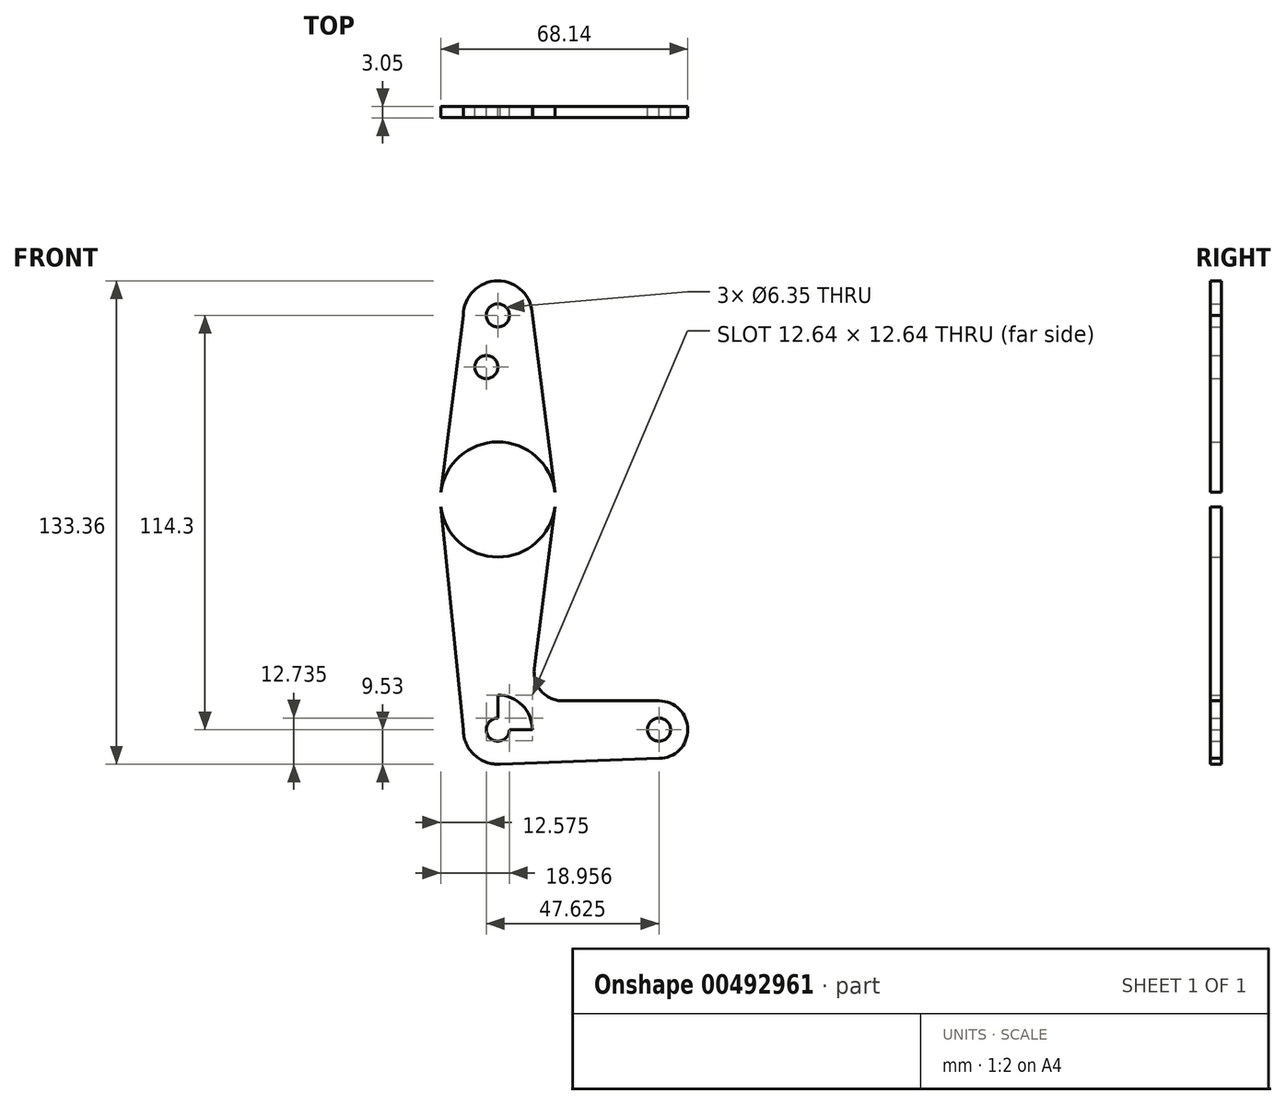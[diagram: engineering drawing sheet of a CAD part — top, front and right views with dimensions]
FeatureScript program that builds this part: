
annotation { "Feature Type Name" : "Feature", "Feature Type Description" : "" }
export const myFeature = defineFeature(function(context is Context, id is Id, definition is map)
    precondition{}
    {
        {
            var Q0;
            Q0=qCreatedBy(makeId("Front.planeOp"),FACE);
            var sketch = newSketch(context, id + "F0", { "sketchPlane" : qUnion([Q0])});
            skLineSegment(sketch, "E0", {"start": v(0, 0) * mm, "end": v(0, 114.3) * mm});
            skLineSegment(sketch, "E1", {"start": v(0, 114.3) * mm, "end": v(0, 0) * mm});
            skLineSegment(sketch, "E2", {"start": v(0, 0) * mm, "end": v(44.45, 0) * mm});
            skLineSegment(sketch, "E3", {"start": v(44.45, 0) * mm, "end": v(0, 0) * mm});
            skCircle(sketch, "E4", {"center": v(0, 114.3) * mm, "radius": 9.53 * mm});
            skCircle(sketch, "E5", {"center": v(0, 63.5) * mm, "radius": 15.88 * mm});
            skCircle(sketch, "E6", {"center": v(0, 0) * mm, "radius": 9.53 * mm});
            skCircle(sketch, "E7", {"center": v(44.45, 0) * mm, "radius": 7.94 * mm});
            skLineSegment(sketch, "E8", {"start": v(9.52, 114.3) * mm, "end": v(15.75, 65.5) * mm});
            skLineSegment(sketch, "E9", {"start": v(15.75, 61.5) * mm, "end": v(10.06, 16.9) * mm});
            skLineSegment(sketch, "E10", {"start": v(-9.52, 114.3) * mm, "end": v(-15.75, 65.5) * mm});
            skLineSegment(sketch, "E11", {"start": v(17.95, 7.94) * mm, "end": v(44.45, 7.94) * mm});
            skLineSegment(sketch, "E12", {"start": v(0, -9.53) * mm, "end": v(0.68, -9.5) * mm});
            skLineSegment(sketch, "E13", {"start": v(-15.75, 61.5) * mm, "end": v(-9.53, 0) * mm});
            skLineSegment(sketch, "E14", {"start": v(0.68, -9.5) * mm, "end": v(44.45, -7.94) * mm});
            skCircle(sketch, "E15", {"center": v(0, 114.3) * mm, "radius": 3.18 * mm});
            skCircle(sketch, "E16", {"center": v(-3.17, 100.03) * mm, "radius": 3.18 * mm});
            skCircle(sketch, "E17", {"center": v(0, 63.5) * mm, "radius": 3.17 * mm});
            skCircle(sketch, "E18", {"center": v(0, 0) * mm, "radius": 3.18 * mm});
            skCircle(sketch, "E19", {"center": v(44.45, 0) * mm, "radius": 3.18 * mm});
            skArc(sketch, "E20.filletArc", {"start": v(10.06, 16.9) * mm, "mid": v(11.98, 10.63) * mm, "end": v(17.95, 7.94) * mm});
            skSolve(sketch);
        }
        {
            var Q0;
            {var subQ0=sQuery(id+"F0.wireOp",EDGE,"E12");Q0=makeQuery(id+"F0.imprint","IMPRINT",FACE,{"disambiguationData":[TD([[makeQuery(id+"F0.imprint","IMPRINT",EDGE,{"derivedFrom":subQ0}),-1.0]])]});}
            var Q1;
            {var subQ5=sQuery(id+"F0.wireOp",EDGE,"E13");Q1=makeQuery(id+"F0.imprint","IMPRINT",FACE,{"disambiguationData":[TD([[makeQuery(id+"F0.imprint","IMPRINT",EDGE,{"derivedFrom":subQ5}),1.0]])]});}
            var Q2;
            {var subQ5=sQuery(id+"F0.wireOp",EDGE,"E14");Q2=makeQuery(id+"F0.imprint","IMPRINT",FACE,{"disambiguationData":[TD([[makeQuery(id+"F0.imprint","IMPRINT",EDGE,{"derivedFrom":subQ5}),1.0]])]});}
            var Q3;
            Q3=makeQuery(id+"F0.imprint","IMPRINT",FACE,{"disambiguationData":[TD([[makeQuery(id+"F0.imprint","IMPRINT",EDGE,{"derivedFrom":sQuery(id+"F0.wireOp",EDGE,"E15")}),-1.0]])]});
            var Q4;
            Q4=makeQuery(id+"F0.imprint","IMPRINT",FACE,{"disambiguationData":[TD([[makeQuery(id+"F0.imprint","IMPRINT",EDGE,{"derivedFrom":sQuery(id+"F0.wireOp",EDGE,"E19")}),-1.0]])]});
            var Q5;
            {var subQ0=sQuery(id+"F0.wireOp",EDGE,"E10");Q5=makeQuery(id+"F0.imprint","IMPRINT",FACE,{"disambiguationData":[TD([[makeQuery(id+"F0.imprint","IMPRINT",EDGE,{"derivedFrom":subQ0}),1.0]])]});}
            var Q6;
            {var subQ0=sQuery(id+"F0.wireOp",EDGE,"E5");var subQ2=sQuery(id+"F0.wireOp",EDGE,"E1");var subQ5=makeQuery(id+"F0.imprint","INTERSECT",VERTEX,{"disambiguationData":[OD(0.0)],"derivedFrom":[subQ2,subQ0]});Q6=makeQuery(id+"F0.imprint","IMPRINT",FACE,{"disambiguationData":[TD([[makeQuery(id+"F0.imprint","IMPRINT",EDGE,{"disambiguationData":[TD([[subQ5,-1.0]])],"derivedFrom":subQ2}),1.0]])]});}
            var Q7;
            {var subQ0=sQuery(id+"F0.wireOp",EDGE,"E5");var subQ3=sQuery(id+"F0.wireOp",EDGE,"E1");var subQ4=makeQuery(id+"F0.imprint","INTERSECT",VERTEX,{"disambiguationData":[OD(0.0)],"derivedFrom":[subQ3,subQ0]});Q7=makeQuery(id+"F0.imprint","IMPRINT",FACE,{"disambiguationData":[TD([[makeQuery(id+"F0.imprint","IMPRINT",EDGE,{"disambiguationData":[TD([[subQ4,-1.0]])],"derivedFrom":subQ3}),-1.0]])]});}
            var Q8;
            {var subQ0=sQuery(id+"F0.wireOp",EDGE,"E9");Q8=makeQuery(id+"F0.imprint","IMPRINT",FACE,{"disambiguationData":[TD([[makeQuery(id+"F0.imprint","IMPRINT",EDGE,{"derivedFrom":subQ0}),-1.0]])]});}
            var Q9;
            {var subQ0=sQuery(id+"F0.wireOp",EDGE,"E12");Q9=makeQuery(id+"F0.imprint","IMPRINT",FACE,{"disambiguationData":[TD([[makeQuery(id+"F0.imprint","IMPRINT",EDGE,{"derivedFrom":subQ0}),1.0]])]});}
            var Q10;
            {var subQ0=sQuery(id+"F0.wireOp",EDGE,"E6");var subQ1=sQuery(id+"F0.wireOp",EDGE,"E1");var subQ2=makeQuery(id+"F0.imprint","INTERSECT",VERTEX,{"derivedFrom":[subQ1,subQ0]});Q10=makeQuery(id+"F0.imprint","IMPRINT",FACE,{"disambiguationData":[TD([[makeQuery(id+"F0.imprint","IMPRINT",EDGE,{"disambiguationData":[TD([[subQ2,-1.0]])],"derivedFrom":subQ1}),1.0]])]});}
            var Q11;
            {var subQ0=sQuery(id+"F0.wireOp",EDGE,"E8");Q11=makeQuery(id+"F0.imprint","IMPRINT",FACE,{"disambiguationData":[TD([[makeQuery(id+"F0.imprint","IMPRINT",EDGE,{"derivedFrom":subQ0}),-1.0]])]});}
            extrude(context, id + "F1", {"entities" : qUnion([Q0, Q1, Q2, Q3, Q4, Q5, Q6, Q7, Q8, Q9, Q10, Q11]), "depth" : 3.05 * mm});
        }
    });
